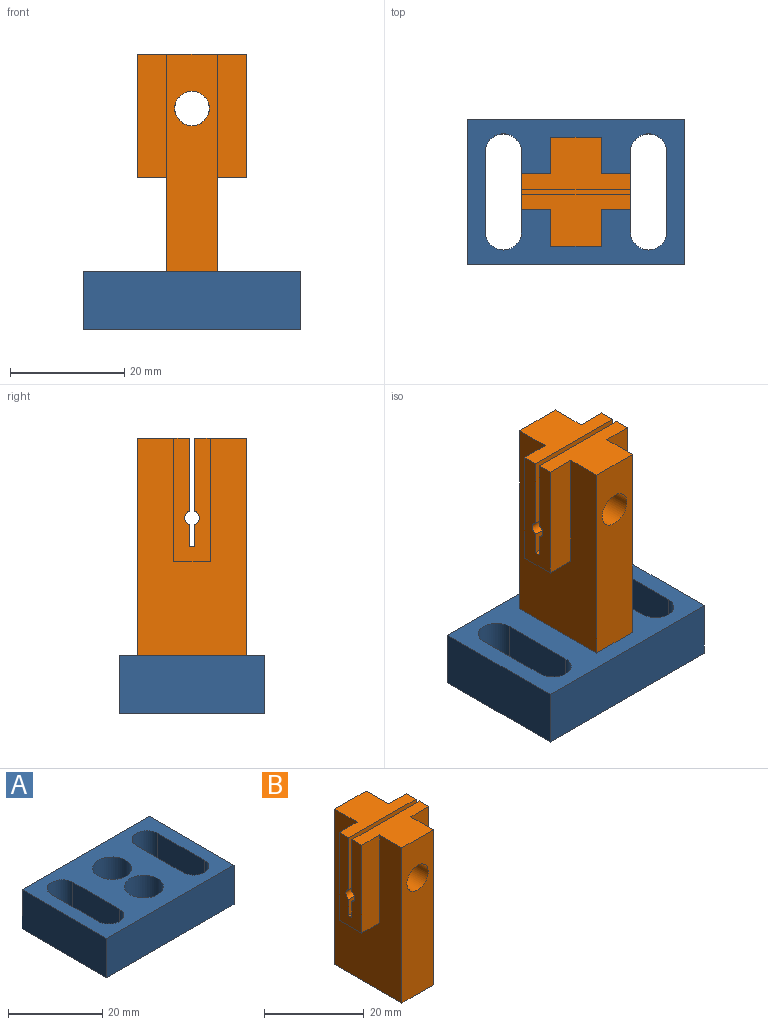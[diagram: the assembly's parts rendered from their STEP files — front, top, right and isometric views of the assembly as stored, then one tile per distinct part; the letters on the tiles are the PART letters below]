
ASSEMBLY  parts=2 mates=1
PART A: 20 faces, bbox 38.1x25.4x10.2 mm
  f0: plane 38.1x10.16mm, normal (0,-1,0), area 387.1mm2, adj f1,f11,f12,f13
  f1: plane 25.4x10.16mm, normal (1,0,0), area 258.1mm2, adj f0,f2,f12,f13
  f2: plane 38.1x10.16mm, normal (0,1,0), area 387.1mm2, adj f1,f11,f12,f13
  f3: cylinder r=3.17mm len=10.16mm, axis (0,0,1), area 101.3mm2, adj f4,f9,f12,f13
  f4: plane 13.97x10.16mm, normal (-1,0,0), area 141.9mm2, adj f3,f5,f12,f13
  f5: cylinder r=3.17mm len=10.16mm, axis (0,0,1), area 101.3mm2, adj f4,f9,f12,f13
  f6: cylinder r=3.17mm len=10.16mm, axis (0,0,1), area 101.3mm2, adj f7,f10,f12,f13
  f7: plane 13.97x10.16mm, normal (1,0,0), area 141.9mm2, adj f6,f8,f12,f13
  f8: cylinder r=3.17mm len=10.16mm, axis (0,0,1), area 101.3mm2, adj f7,f10,f12,f13
  f9: plane 13.97x10.16mm, normal (1,0,0), area 141.9mm2, adj f3,f5,f12,f13
  f10: plane 13.97x10.16mm, normal (-1,0,0), area 141.9mm2, adj f6,f8,f12,f13
  f11: plane 25.4x10.16mm, normal (-1,0,0), area 258.1mm2, adj f0,f2,f12,f13
  f12: plane 38.1x25.4mm, normal (0,0,-1), area 686.4mm2, adj f0,f1,f2,f3,f4,f5,f6,f7
  f13: plane 38.1x25.4mm, normal (0,0,1), area 619.9mm2, adj f0,f1,f2,f3,f4,f5,f6,f7
  f14: cylinder r=2.54mm len=5.08mm, axis (0,0,1), area 40.5mm2, adj f12,f15
  f15: plane 8.26x8.26mm, normal (0,0,1), area 33.3mm2, adj f14,f16
  f16: cylinder r=4.13mm len=8.26mm, axis (0,0,1), area 197.6mm2, adj f13,f15
  f17: cylinder r=2.54mm len=5.08mm, axis (0,0,1), area 40.5mm2, adj f12,f18
  f18: plane 8.26x8.26mm, normal (0,0,1), area 33.3mm2, adj f17,f19
  f19: cylinder r=4.13mm len=8.26mm, axis (0,0,1), area 197.6mm2, adj f13,f18
PART B: 28 faces, bbox 19.1x19.1x38.1 mm
  f0: plane 19.05x9.08mm, normal (0,0,1), area 108.5mm2, adj f1,f4,f6,f9,f22,f23,f25,f26
  f1: plane 38.1x8.89mm, normal (0,-1,0), area 310mm2, adj f0,f8,f21,f22,f23
  f2: plane 38.1x8.89mm, normal (0,1,0), area 310mm2, adj f3,f8,f20,f22,f23
  f3: plane 19.05x9.08mm, normal (0,0,1), area 108.5mm2, adj f2,f4,f6,f10,f22,f23,f24,f27
  f4: plane 21.59x6.35mm, normal (-1,0,0), area 117.3mm2, adj f0,f3,f5,f9,f10,f11,f12,f13
  f5: plane 6.35x5.08mm, normal (0,0,-1), area 32.3mm2, adj f4,f23,f26,f27
  f6: plane 21.59x6.35mm, normal (1,0,0), area 117.3mm2, adj f0,f3,f7,f9,f10,f11,f12,f13
  f7: plane 6.35x5.08mm, normal (0,0,-1), area 32.3mm2, adj f6,f22,f24,f25
  f8: plane 19.05x8.89mm, normal (0,0,-1), area 128.8mm2, adj f1,f2,f16,f18,f22,f23
  f9: plane 19.05x12.78mm, normal (0,1,0), area 214.8mm2, adj f0,f4,f6,f15,f21
  f10: plane 19.05x12.78mm, normal (0,-1,0), area 214.8mm2, adj f3,f4,f6,f11,f20
  f11: cylinder r=1.27mm len=19.05mm, axis (1,0,0), area 58.7mm2, adj f4,f6,f10,f12
  f12: plane 19.05x3.89mm, normal (0,-1,0), area 74.1mm2, adj f4,f6,f11,f13
  f13: plane 19.05x0.89mm, normal (0,0,1), area 16.9mm2, adj f4,f6,f12,f14
  f14: plane 19.05x3.89mm, normal (0,1,0), area 74.1mm2, adj f4,f6,f13,f15
  f15: cylinder r=1.27mm len=19.05mm, axis (1,0,0), area 58.7mm2, adj f4,f6,f9,f14
  f16: cylinder r=2.54mm len=10.16mm, axis (0,0,-1), area 162.1mm2, adj f8,f17
  f17: plane 5.08x5.08mm, normal (0,0,-1), area 20.3mm2, adj f16
  f18: cylinder r=2.54mm len=10.16mm, axis (0,0,-1), area 162.1mm2, adj f8,f19
  f19: plane 5.08x5.08mm, normal (0,0,-1), area 20.3mm2, adj f18
  f20: cylinder r=3.02mm len=9.08mm, axis (0,1,0), area 172.5mm2, adj f2,f10
  f21: cylinder r=3.02mm len=9.08mm, axis (0,1,0), area 172.5mm2, adj f1,f9
  f22: plane 38.1x19.05mm, normal (1,0,0), area 588.7mm2, adj f0,f1,f2,f3,f7,f8,f24,f25
  f23: plane 38.1x19.05mm, normal (-1,0,0), area 588.7mm2, adj f0,f1,f2,f3,f5,f8,f26,f27
  f24: plane 21.59x5.08mm, normal (0,1,0), area 109.7mm2, adj f3,f6,f7,f22
  f25: plane 21.59x5.08mm, normal (0,-1,0), area 109.7mm2, adj f0,f6,f7,f22
  f26: plane 21.59x5.08mm, normal (0,-1,0), area 109.7mm2, adj f0,f4,f5,f23
  f27: plane 21.59x5.08mm, normal (0,1,0), area 109.7mm2, adj f3,f4,f5,f23
PLACE A rot(axis=(1,0,0),180deg) t=(-6.36,31.75,21.38)mm
PLACE B t=(-15.89,28.58,31.54)mm
MATE cylindrical A.f17 <-> B.f18  axis (0,0,1) through (-25.41,14.29,31.54)mm
